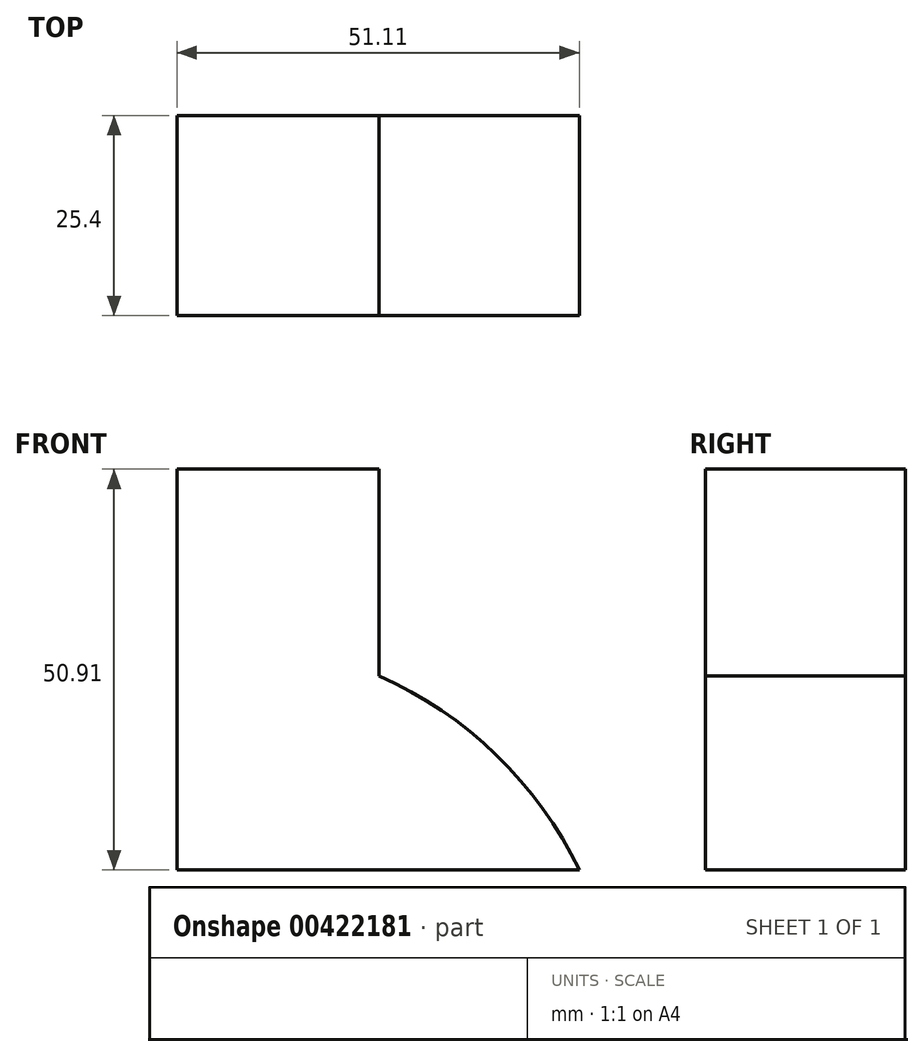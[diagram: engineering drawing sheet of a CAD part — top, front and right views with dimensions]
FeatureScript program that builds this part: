
annotation { "Feature Type Name" : "Feature", "Feature Type Description" : "" }
export const myFeature = defineFeature(function(context is Context, id is Id, definition is map)
    precondition{}
    {
        {
            var Q0;
            Q0=qCreatedBy(makeId("Front.planeOp"),FACE);
            var sketch = newSketch(context, id + "F0", { "sketchPlane" : qUnion([Q0])});
            skLineSegment(sketch, "E0", {"start": v(-72.9, 43.5) * mm, "end": v(-47.26, 43.5) * mm});
            skLineSegment(sketch, "E1", {"start": v(-72.9, 43.5) * mm, "end": v(-72.9, -7.4) * mm});
            skLineSegment(sketch, "E2", {"start": v(-72.9, -7.4) * mm, "end": v(-21.8, -7.4) * mm});
            skLineSegment(sketch, "E3", {"start": v(-47.26, 43.5) * mm, "end": v(-47.26, 17.26) * mm});
            skArc(sketch, "E4", {"start": v(-21.8, -7.4) * mm, "mid": v(-32.35, 7.18) * mm, "end": v(-47.26, 17.26) * mm});
            skSolve(sketch);
        }
        {
            var Q0;
            Q0=makeQuery(id+"F0.imprint","IMPRINT",FACE,{"disambiguationData":[TD([[makeQuery(id+"F0.imprint","IMPRINT",EDGE,{"derivedFrom":sQuery(id+"F0.wireOp",EDGE,"E0")}),-1.0]])]});
            extrude(context, id + "F1", {"entities" : qUnion([Q0]), "depth" : 25.4 * mm});
        }
    });
